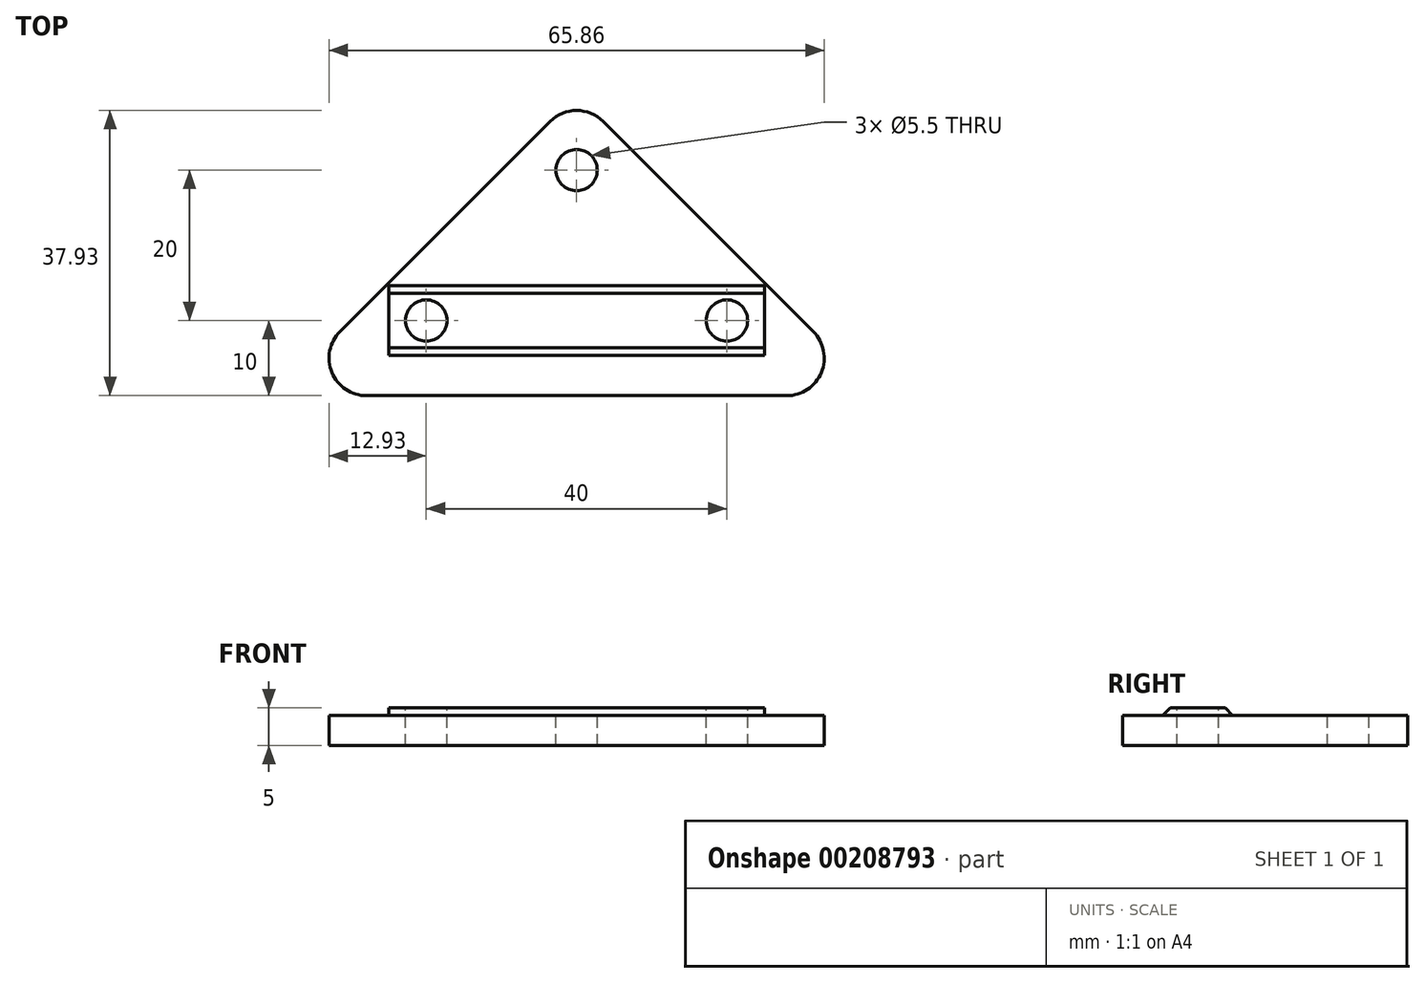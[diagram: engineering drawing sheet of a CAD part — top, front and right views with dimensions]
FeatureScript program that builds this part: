
annotation { "Feature Type Name" : "Feature", "Feature Type Description" : "" }
export const myFeature = defineFeature(function(context is Context, id is Id, definition is map)
    precondition{}
    {
        {
            var Q0;
            Q0=qCreatedBy(makeId("Top.planeOp"),FACE);
            var sketch = newSketch(context, id + "F0", { "sketchPlane" : qUnion([Q0])});
            skLineSegment(sketch, "E0", {"start": v(-3.54, 36.46) * mm, "end": v(-31.46, 8.54) * mm});
            skLineSegment(sketch, "E1", {"start": v(-27.93, 0) * mm, "end": v(27.93, 0) * mm});
            skLineSegment(sketch, "E2", {"start": v(31.46, 8.54) * mm, "end": v(3.54, 36.46) * mm});
            skPoint(sketch, "E3", {"position": v(-20, 10) * mm});
            skPoint(sketch, "E4", {"position": v(20, 10) * mm});
            skPoint(sketch, "E5", {"position": v(0, 30) * mm});
            skPoint(sketch, "E6.visualSharp", {"position": v(-40, 0) * mm});
            skArc(sketch, "E6.filletArc", {"start": v(-31.46, 8.54) * mm, "mid": v(-32.55, 3.09) * mm, "end": v(-27.93, 0) * mm});
            skPoint(sketch, "E7.visualSharp", {"position": v(0, 40) * mm});
            skArc(sketch, "E7.filletArc", {"start": v(3.54, 36.46) * mm, "mid": v(0, 37.93) * mm, "end": v(-3.54, 36.46) * mm});
            skPoint(sketch, "E8.visualSharp", {"position": v(40, 0) * mm});
            skArc(sketch, "E8.filletArc", {"start": v(27.93, 0) * mm, "mid": v(32.55, 3.09) * mm, "end": v(31.46, 8.54) * mm});
            skSolve(sketch);
        }
        {
            var Q0;
            Q0=makeQuery(id+"F0.imprint","IMPRINT",FACE,{"disambiguationData":[TD([[makeQuery(id+"F0.imprint","IMPRINT",EDGE,{"derivedFrom":sQuery(id+"F0.wireOp",EDGE,"E0")}),1.0]])]});
            extrude(context, id + "F1", {"entities" : qUnion([Q0]), "depth" : 4 * mm});
        }
        {
            var Q0;
            Q0=qCreatedBy(makeId("Right.planeOp"),FACE);
            var sketch = newSketch(context, id + "F2", { "sketchPlane" : qUnion([Q0])});
            skLineSegment(sketch, "E9", {"start": v(0, 0) * mm, "end": v(20, 0) * mm, "construction": true});
            skLineSegment(sketch, "E10", {"start": v(20, 0) * mm, "end": v(20, 4) * mm, "construction": true});
            skLineSegment(sketch, "E11", {"start": v(20, 4) * mm, "end": v(14.64, 4) * mm, "construction": true});
            skLineSegment(sketch, "E12", {"start": v(14.64, 4) * mm, "end": v(13.64, 5) * mm});
            skLineSegment(sketch, "E13", {"start": v(13.64, 5) * mm, "end": v(12.84, 5.8) * mm, "construction": true});
            skLineSegment(sketch, "E14", {"start": v(12.84, 5.8) * mm, "end": v(7.16, 5.8) * mm, "construction": true});
            skLineSegment(sketch, "E15", {"start": v(7.16, 5.8) * mm, "end": v(6.36, 5) * mm, "construction": true});
            skLineSegment(sketch, "E16", {"start": v(6.36, 5) * mm, "end": v(5.36, 4) * mm});
            skLineSegment(sketch, "E17", {"start": v(5.36, 4) * mm, "end": v(0, 4) * mm, "construction": true});
            skLineSegment(sketch, "E18", {"start": v(0, 4) * mm, "end": v(0, 0) * mm, "construction": true});
            skLineSegment(sketch, "E19", {"start": v(14.64, 4) * mm, "end": v(5.36, 4) * mm});
            skLineSegment(sketch, "E20", {"start": v(7.16, 5.8) * mm, "end": v(10, 8.64) * mm, "construction": true});
            skLineSegment(sketch, "E21", {"start": v(10, 8.64) * mm, "end": v(12.84, 5.8) * mm, "construction": true});
            skLineSegment(sketch, "E22", {"start": v(13.64, 5) * mm, "end": v(6.36, 5) * mm});
            skSolve(sketch);
        }
        {
            var Q0;
            Q0=qSketchRegion(id+"F2",true);
            var Q1;
            Q1=makeQuery(id+"F1.opExtrude","SWEPT_FACE",FACE,{"disambiguationData":[OSD([sQuery(id+"F0.wireOp",EDGE,"E2")])]});
            var Q2;
            Q2=makeQuery(id+"F1.opExtrude","SWEPT_BODY",BODY,{"disambiguationData":[OSD([sQuery(id+"F0.wireOp",EDGE,"E0"),sQuery(id+"F0.wireOp",EDGE,"E1"),sQuery(id+"F0.wireOp",EDGE,"E2"),sQuery(id+"F0.wireOp",EDGE,"E6.filletArc"),sQuery(id+"F0.wireOp",EDGE,"E7.filletArc"),sQuery(id+"F0.wireOp",EDGE,"E8.filletArc")])]});
            var Q3;
            Q3=makeQuery(id+"F1.opExtrude","SWEPT_FACE",FACE,{"disambiguationData":[OSD([sQuery(id+"F0.wireOp",EDGE,"E0")])]});
            var Q4;
            Q4=makeQuery(id+"F1.opExtrude","SWEPT_BODY",BODY,{"disambiguationData":[OSD([sQuery(id+"F0.wireOp",EDGE,"E0"),sQuery(id+"F0.wireOp",EDGE,"E1"),sQuery(id+"F0.wireOp",EDGE,"E2"),sQuery(id+"F0.wireOp",EDGE,"E6.filletArc"),sQuery(id+"F0.wireOp",EDGE,"E7.filletArc"),sQuery(id+"F0.wireOp",EDGE,"E8.filletArc")])]});
            extrude(context, id + "F3", {"entities" : qUnion([Q0]), "operationType" : NewBodyOperationType.ADD, "endBoundEntityFace" : qUnion([Q1]), "endBoundEntityBody" : qUnion([Q2]), "depth" : 25 * mm, "hasSecondDirection" : true, "secondDirectionOppositeDirection" : true, "secondDirectionBoundEntityFace" : qUnion([Q3]), "secondDirectionBoundEntityBody" : qUnion([Q4]), "secondDirectionDepth" : 25 * mm});
        }
        {
            var Q0;
            Q0=sQuery(id+"F0.wireOp",VERTEX,"E3");
            var Q1;
            Q1=sQuery(id+"F0.wireOp",VERTEX,"E5");
            var Q2;
            Q2=sQuery(id+"F0.wireOp",VERTEX,"E4");
            var Q3;
            Q3=makeQuery(id+"F1.opExtrude","SWEPT_BODY",BODY,{"disambiguationData":[OSD([sQuery(id+"F0.wireOp",EDGE,"E0"),sQuery(id+"F0.wireOp",EDGE,"E1"),sQuery(id+"F0.wireOp",EDGE,"E2")])]});
            hole(context, id + "F4", {"style" : HoleStyle.SIMPLE, "endStyle" : HoleEndStyle.THROUGH, "oppositeDirection" : true, "standardTappedOrClearance" : lookupTablePath({ "standard" : "ISO", "fit" : "Normal", "size" : "M5", "type" : "Clearance" }), "standardBlindInLast" : lookupTablePath({ "fit" : "Standard", "standard" : "ISO", "size" : "M5", "type" : "Clearance" }), "holeDiameter" : 5.5 * mm, "locations" : qUnion([Q0, Q1, Q2]), "scope" : qUnion([Q3]), "isTappedThrough" : true});
        }
    });
